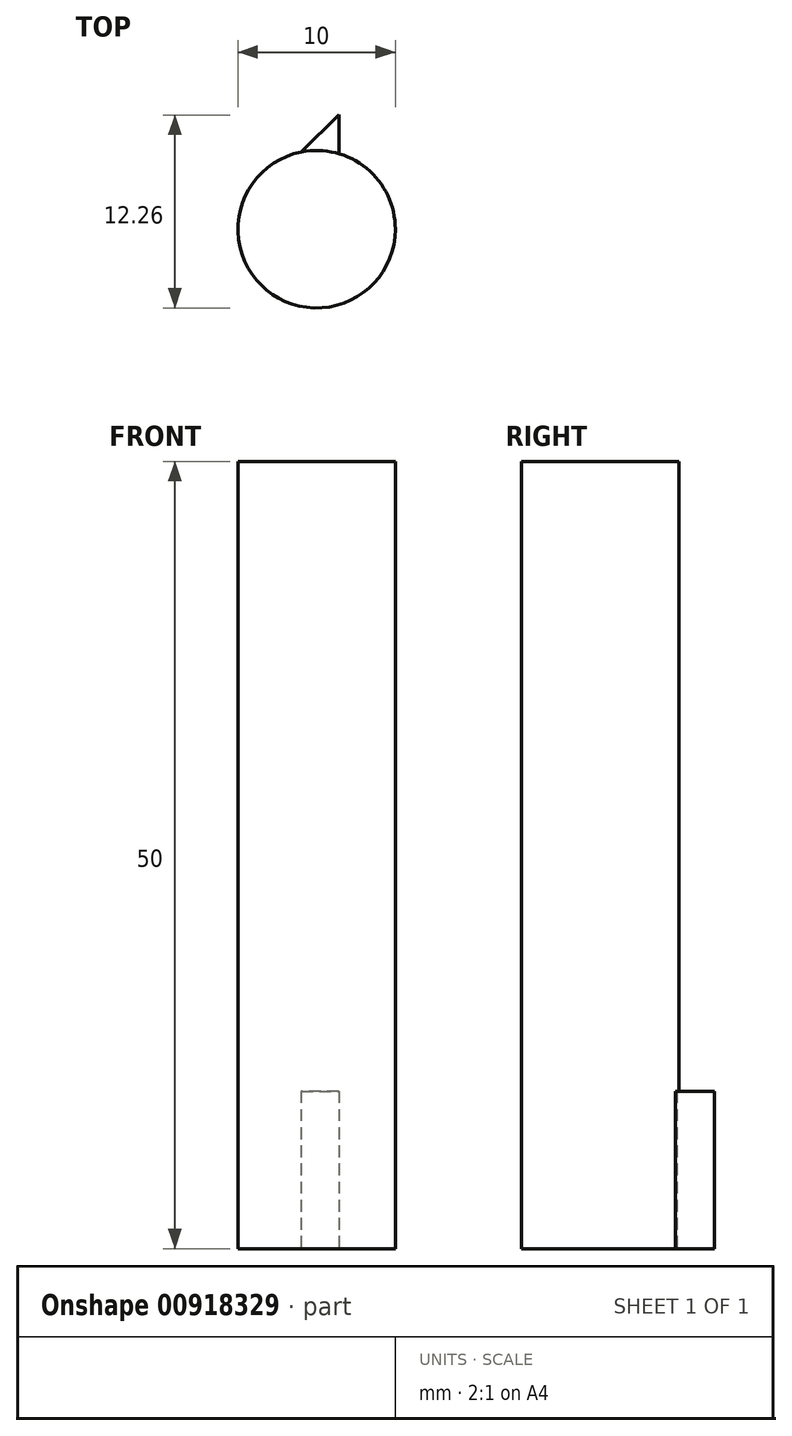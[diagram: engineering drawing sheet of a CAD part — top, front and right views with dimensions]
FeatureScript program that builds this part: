
annotation { "Feature Type Name" : "Feature", "Feature Type Description" : "" }
export const myFeature = defineFeature(function(context is Context, id is Id, definition is map)
    precondition{}
    {
        {
            var Q0;
            Q0=qCreatedBy(makeId("Top.planeOp"),FACE);
            var sketch = newSketch(context, id + "F0", { "sketchPlane" : qUnion([Q0])});
            skCircle(sketch, "E0", {"center": v(0, 0) * mm, "radius": 5 * mm});
            skLineSegment(sketch, "E1", {"start": v(0, 0) * mm, "end": v(-0.98, 4.9) * mm});
            skLineSegment(sketch, "E2", {"start": v(-0.98, 4.9) * mm, "end": v(1.42, 7.26) * mm});
            skLineSegment(sketch, "E3", {"start": v(1.42, 7.26) * mm, "end": v(1.42, 4.8) * mm});
            skLineSegment(sketch, "E4", {"start": v(1.42, 4.8) * mm, "end": v(0, 0) * mm});
            skSolve(sketch);
        }
        {
            var Q0;
            {var subQ0=sQuery(id+"F0.wireOp",EDGE,"E1");Q0=makeQuery(id+"F0.imprint","IMPRINT",FACE,{"disambiguationData":[TD([[makeQuery(id+"F0.imprint","IMPRINT",EDGE,{"derivedFrom":subQ0}),1.0]])]});}
            var Q1;
            {var subQ0=sQuery(id+"F0.wireOp",EDGE,"E1");Q1=makeQuery(id+"F0.imprint","IMPRINT",FACE,{"disambiguationData":[TD([[makeQuery(id+"F0.imprint","IMPRINT",EDGE,{"derivedFrom":subQ0}),-1.0]])]});}
            var Q2;
            {var subQ0=sQuery(id+"F0.wireOp",EDGE,"E2");Q2=makeQuery(id+"F0.imprint","IMPRINT",FACE,{"disambiguationData":[TD([[makeQuery(id+"F0.imprint","IMPRINT",EDGE,{"derivedFrom":subQ0}),-1.0]])]});}
            extrude(context, id + "F1", {"entities" : qUnion([Q0, Q1, Q2]), "depth" : 10 * mm, "offsetDistance" : 25 * mm});
        }
        {
            var Q0;
            Q0=makeQuery(id+"F1.opExtrude","CAP_FACE",FACE,{"disambiguationData":[OSD([sQuery(id+"F0.wireOp",EDGE,"E0"),sQuery(id+"F0.wireOp",EDGE,"E2"),sQuery(id+"F0.wireOp",EDGE,"E3")])],"isStart":false});
            var sketch = newSketch(context, id + "F2", { "sketchPlane" : qUnion([Q0])});
            skCircle(sketch, "E5", {"center": v(0, 0) * mm, "radius": 5 * mm});
            skSolve(sketch);
        }
        {
            var Q0;
            {var subQ0=sQuery(id+"F2.wireOp",EDGE,"E5");var subQ1=makeQuery(id+"F2.imprint","INTERSECT",VERTEX,{"derivedFrom":[makeQuery(id+"F1.opExtrude","CAP_EDGE",EDGE,{"disambiguationData":[OSD([sQuery(id+"F0.wireOp",EDGE,"E2")])],"isStart":false}),subQ0]});Q0=makeQuery(id+"F2.imprint","IMPRINT",FACE,{"disambiguationData":[TD([[makeQuery(id+"F2.imprint","IMPRINT",EDGE,{"disambiguationData":[TD([[subQ1,1.0]])],"derivedFrom":subQ0}),1.0]])]});}
            extrude(context, id + "F3", {"entities" : qUnion([Q0]), "operationType" : NewBodyOperationType.ADD, "depth" : 40 * mm, "offsetDistance" : 25 * mm});
        }
    });
